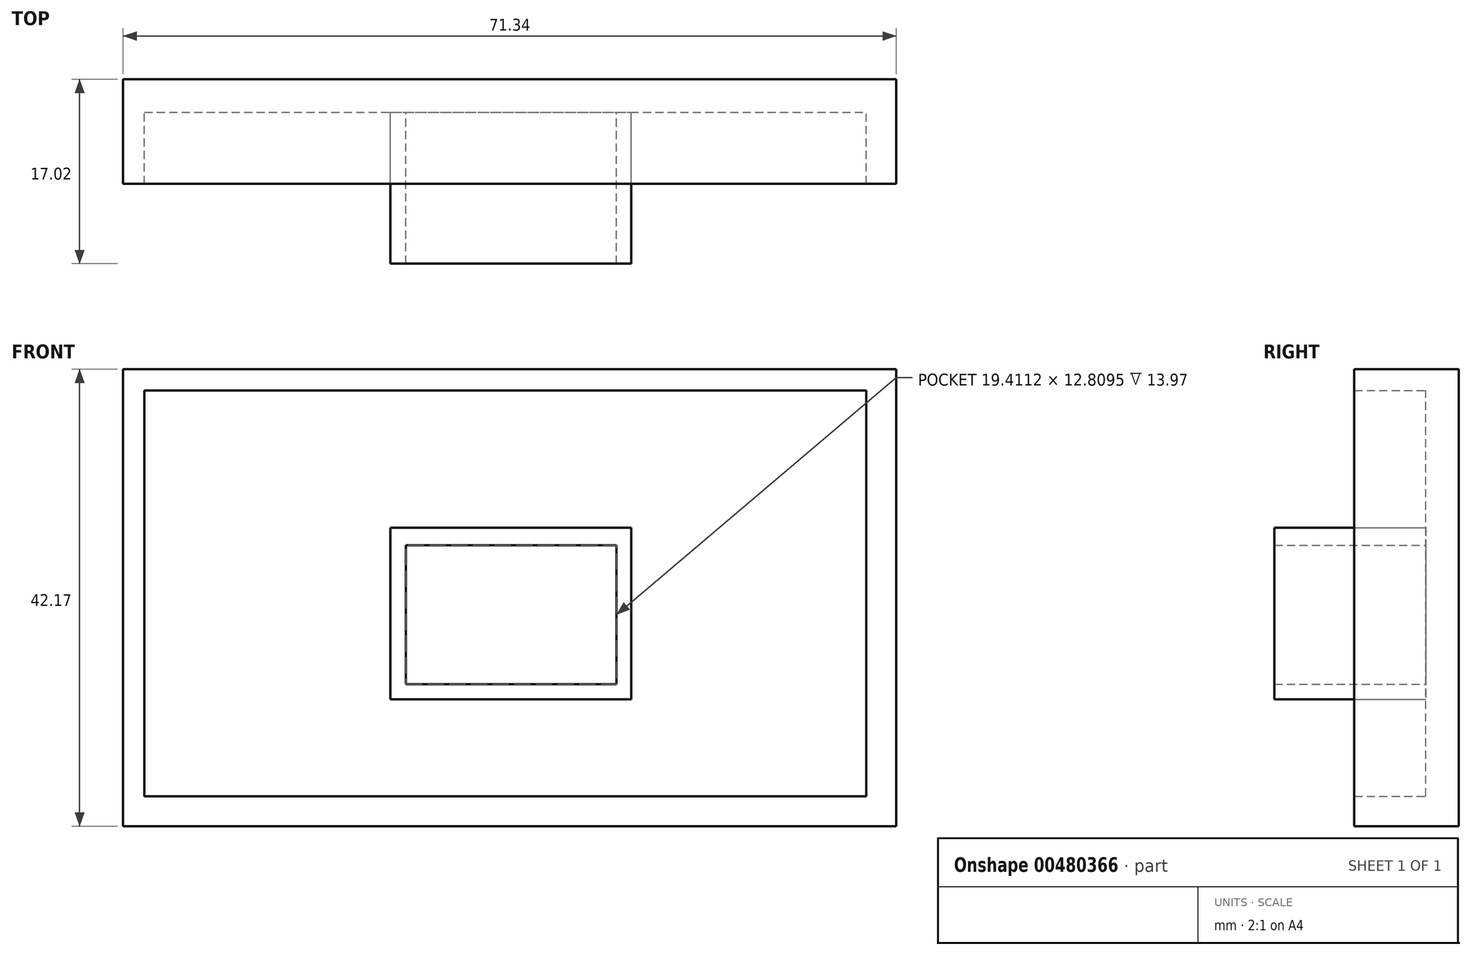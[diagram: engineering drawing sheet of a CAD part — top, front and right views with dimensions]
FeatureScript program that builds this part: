
annotation { "Feature Type Name" : "Feature", "Feature Type Description" : "" }
export const myFeature = defineFeature(function(context is Context, id is Id, definition is map)
    precondition{}
    {
        {
            var Q0;
            Q0=qCreatedBy(makeId("Front.planeOp"),FACE);
            var sketch = newSketch(context, id + "F0", { "sketchPlane" : qUnion([Q0])});
            skLineSegment(sketch, "E0.bottom", {"start": v(-38.82, 24.63) * mm, "end": v(32.52, 24.63) * mm});
            skLineSegment(sketch, "E0.top", {"start": v(-38.82, -17.54) * mm, "end": v(32.52, -17.54) * mm});
            skLineSegment(sketch, "E0.left", {"start": v(-38.82, 24.63) * mm, "end": v(-38.82, -17.54) * mm});
            skLineSegment(sketch, "E0.right", {"start": v(32.52, 24.63) * mm, "end": v(32.52, -17.54) * mm});
            skSolve(sketch);
        }
        {
            var Q0;
            Q0=makeQuery(id+"F0.imprint","IMPRINT",FACE,{"disambiguationData":[TD([[makeQuery(id+"F0.imprint","IMPRINT",EDGE,{"derivedFrom":sQuery(id+"F0.wireOp",EDGE,"E0.bottom")}),-1.0]])]});
            extrude(context, id + "F1", {"entities" : qUnion([Q0]), "depth" : 3.05 * mm});
        }
        {
            var Q0;
            Q0=makeQuery(id+"F1.opExtrude","CAP_FACE",FACE,{"disambiguationData":[OSD([sQuery(id+"F0.wireOp",EDGE,"E0.bottom"),sQuery(id+"F0.wireOp",EDGE,"E0.top"),sQuery(id+"F0.wireOp",EDGE,"E0.left"),sQuery(id+"F0.wireOp",EDGE,"E0.right")])],"isStart":false});
            var sketch = newSketch(context, id + "F2", { "sketchPlane" : qUnion([Q0])});
            skLineSegment(sketch, "E1", {"start": v(-38.82, 24.63) * mm, "end": v(32.52, 24.63) * mm});
            skLineSegment(sketch, "E2", {"start": v(32.52, 24.63) * mm, "end": v(32.52, -17.54) * mm});
            skLineSegment(sketch, "E3", {"start": v(32.52, -17.54) * mm, "end": v(-38.82, -17.54) * mm});
            skLineSegment(sketch, "E4", {"start": v(-38.82, -17.54) * mm, "end": v(-38.82, 24.63) * mm});
            skLineSegment(sketch, "E5", {"start": v(-36.85, 22.66) * mm, "end": v(29.76, 22.66) * mm});
            skLineSegment(sketch, "E6", {"start": v(29.76, 22.66) * mm, "end": v(29.76, -14.78) * mm});
            skLineSegment(sketch, "E7", {"start": v(29.76, -14.78) * mm, "end": v(-36.85, -14.78) * mm});
            skLineSegment(sketch, "E8", {"start": v(-36.85, -14.78) * mm, "end": v(-36.85, 22.66) * mm});
            skSolve(sketch);
        }
        {
            var Q0;
            Q0=makeQuery(id+"F2.imprint","IMPRINT",FACE,{"disambiguationData":[TD([[makeQuery(id+"F2.imprint","IMPRINT",EDGE,{"derivedFrom":sQuery(id+"F2.wireOp",EDGE,"E1")}),-1.0]])]});
            extrude(context, id + "F3", {"entities" : qUnion([Q0]), "operationType" : NewBodyOperationType.ADD, "depth" : 6.6 * mm});
        }
        {
            var Q0;
            Q0=makeQuery(id+"F1.opExtrude","CAP_FACE",FACE,{"disambiguationData":[OSD([sQuery(id+"F0.wireOp",EDGE,"E0.bottom"),sQuery(id+"F0.wireOp",EDGE,"E0.top"),sQuery(id+"F0.wireOp",EDGE,"E0.left"),sQuery(id+"F0.wireOp",EDGE,"E0.right")])],"isStart":false});
            var sketch = newSketch(context, id + "F4", { "sketchPlane" : qUnion([Q0])});
            skLineSegment(sketch, "E9.bottom", {"start": v(-12.71, 8.38) * mm, "end": v(6.7, 8.38) * mm});
            skLineSegment(sketch, "E9.top", {"start": v(-12.71, -4.43) * mm, "end": v(6.7, -4.43) * mm});
            skLineSegment(sketch, "E9.left", {"start": v(-12.71, 8.38) * mm, "end": v(-12.71, -4.43) * mm});
            skLineSegment(sketch, "E9.right", {"start": v(6.7, 8.38) * mm, "end": v(6.7, -4.43) * mm});
            skLineSegment(sketch, "E10.bottom", {"start": v(-14.16, 10) * mm, "end": v(8.07, 10) * mm});
            skLineSegment(sketch, "E10.top", {"start": v(-14.16, -5.83) * mm, "end": v(8.07, -5.83) * mm});
            skLineSegment(sketch, "E10.left", {"start": v(-14.16, 10) * mm, "end": v(-14.16, -5.83) * mm});
            skLineSegment(sketch, "E10.right", {"start": v(8.07, 10) * mm, "end": v(8.07, -5.83) * mm});
            skSolve(sketch);
        }
        {
            var Q0;
            Q0=makeQuery(id+"F4.imprint","IMPRINT",FACE,{"disambiguationData":[TD([[makeQuery(id+"F4.imprint","IMPRINT",EDGE,{"derivedFrom":sQuery(id+"F4.wireOp",EDGE,"E9.bottom")}),1.0]])]});
            extrude(context, id + "F5", {"entities" : qUnion([Q0]), "operationType" : NewBodyOperationType.ADD, "depth" : 13.97 * mm});
        }
    });
